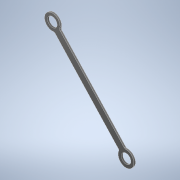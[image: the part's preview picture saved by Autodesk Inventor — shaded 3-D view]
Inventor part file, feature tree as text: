
AUTODESK INVENTOR PART (.ipt)
format: ipt  version: 2022 (Build 260153000, 153)  size: 128,000 bytes
history: native  units: in
note: dims shown in document units (in); Inventor stores cm internally (conversion verified against a paired STEP export)
features: other x1, extrude x1, sketch x1
ambient origin geometry x8: Origin, YZ Plane, XZ Plane, XY Plane, X Axis, Y Axis, Z Axis, Center Point
bodies: Body1 (feature_tree)
feature tree (3):
  other  "Sólido1"
  extrude  "Extrusión1"  Depth=0.0157in
  sketch  "Boceto1"  dims[d7=0.0984in d8=0.1583in d10=0.1606in d11=0.748in d12=0.8268in d14=0.0689in d15=0.0197in d16=0.0157in d17=0.0in]
